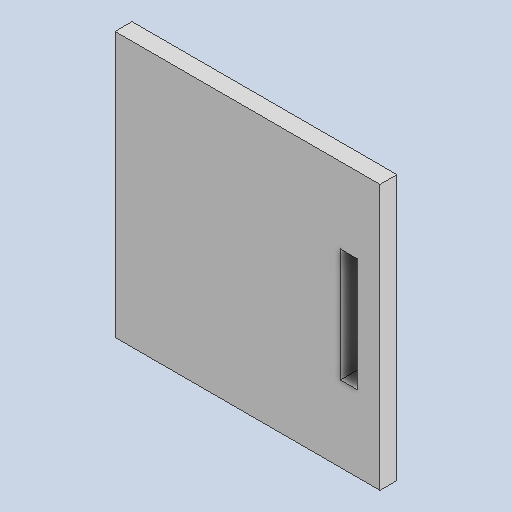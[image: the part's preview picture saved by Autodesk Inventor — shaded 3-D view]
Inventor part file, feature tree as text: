
AUTODESK INVENTOR PART (.ipt)
format: ipt  version: 2022 (Build 260153000, 153)  size: 107,520 bytes
history: native  units: mm
features: other x8, reference x6, extrude x1, sketch x1
ambient origin geometry x8: Origin, YZ Plane, XZ Plane, XY Plane, X Axis, Y Axis, Z Axis, Center Point
bodies: Solid1 (feature_tree)
feature tree (16):
  extrude  "Extrusion1"  Depth=25.0mm
  sketch  "Sketch1"  dims[d2=23.962763mm d3=25.0mm d4=12.5mm d5=5.35mm d6=1.6mm d7=0.0mm]
  reference  "Reference1"
  reference  "Reference2"
  reference  "Reference3"
  reference  "Reference4"
  reference  "Reference5"
  reference  "Reference6"
  other  "<userpath>\Documents\Inventor\NanoSumo\Przekładnia.iam"
  other  "Przekładnia.iam"
  other  "silnik_2:3"
  other  "Spur Gears:2"
  other  "Spur Gear2:1"
  other  "Spur Gears2_MIR1:1"
  other  "Spur Gear22_MIR1:1"
  other  "TOF_VL53L0X (1):1"
